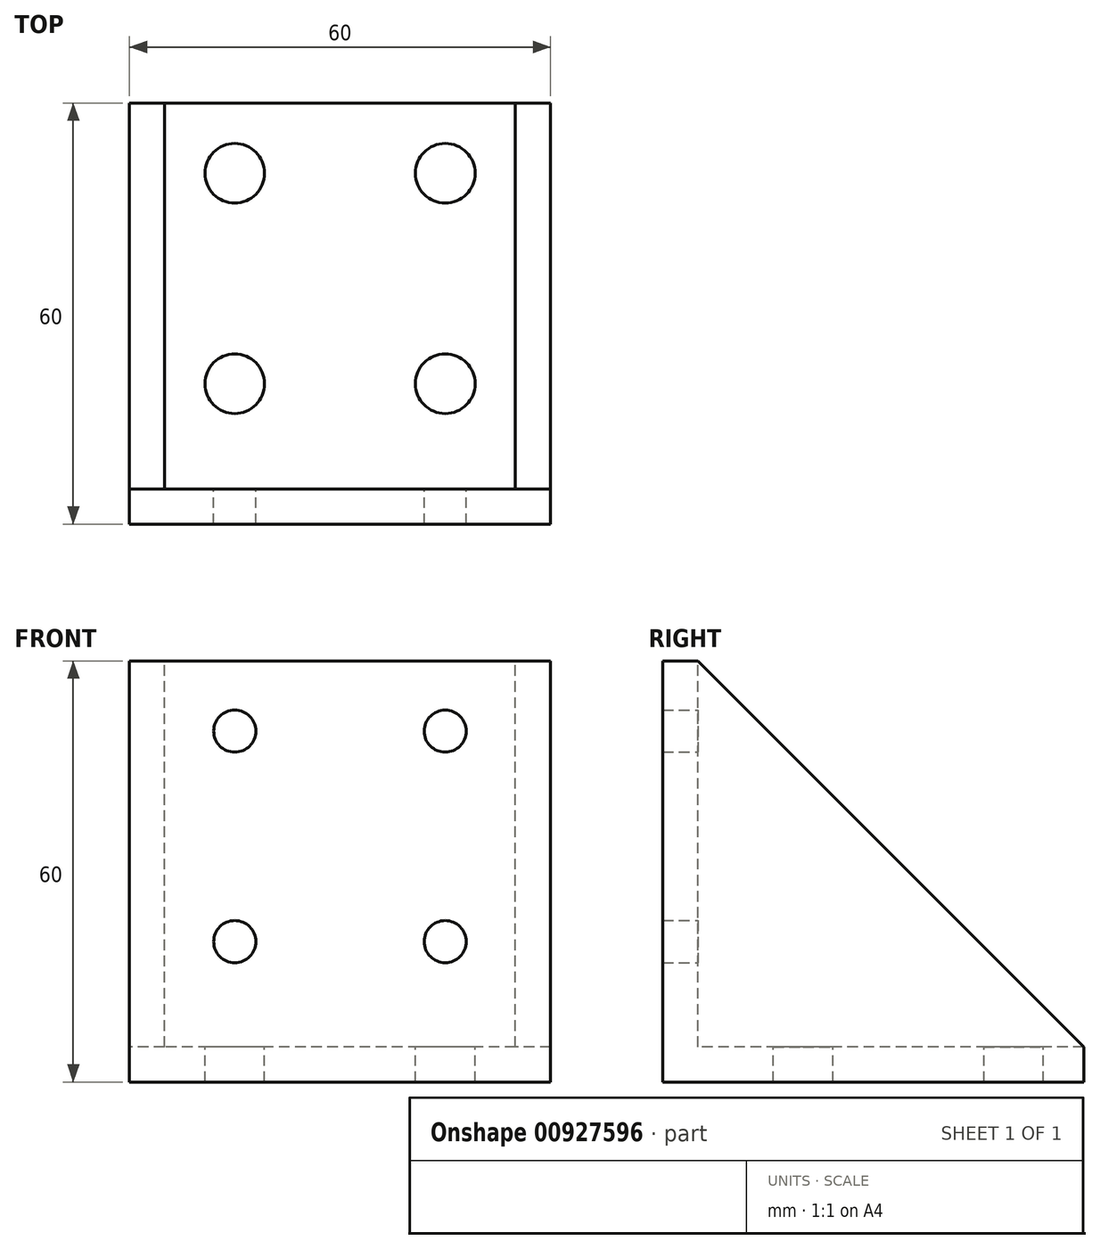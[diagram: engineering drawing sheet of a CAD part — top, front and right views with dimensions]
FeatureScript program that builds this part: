
annotation { "Feature Type Name" : "Feature", "Feature Type Description" : "" }
export const myFeature = defineFeature(function(context is Context, id is Id, definition is map)
    precondition{}
    {
        {
            var Q0;
            Q0=qCreatedBy(makeId("Right.planeOp"),FACE);
            var sketch = newSketch(context, id + "F0", { "sketchPlane" : qUnion([Q0])});
            skLineSegment(sketch, "E0", {"start": v(0, 60) * mm, "end": v(0, 0) * mm});
            skLineSegment(sketch, "E1", {"start": v(0, 0) * mm, "end": v(60, 0) * mm});
            skLineSegment(sketch, "E2.0", {"start": v(5, 60) * mm, "end": v(5, 5) * mm});
            skLineSegment(sketch, "E3.0", {"start": v(5, 5) * mm, "end": v(60, 5) * mm});
            skLineSegment(sketch, "E4", {"start": v(60, 5) * mm, "end": v(60, 0) * mm});
            skLineSegment(sketch, "E5", {"start": v(0, 60) * mm, "end": v(5, 60) * mm});
            skSolve(sketch);
        }
        {
            var Q0;
            Q0 = qSketchRegion(id + "F0", true);
            extrude(context, id + "F1", {"entities" : qUnion([Q0]), "depth" : 60 * mm, "offsetDistance" : 25 * mm});
        }
        {
            var Q0;
            Q0=qCreatedBy(makeId("Right.planeOp"),FACE);
            var sketch = newSketch(context, id + "F2", { "sketchPlane" : qUnion([Q0])});
            skLineSegment(sketch, "E6", {"start": v(5, 60) * mm, "end": v(60, 5) * mm});
            skLineSegment(sketch, "E7", {"start": v(60, 5) * mm, "end": v(5, 5) * mm});
            skLineSegment(sketch, "E8", {"start": v(5, 5) * mm, "end": v(5, 60) * mm});
            skSolve(sketch);
        }
        {
            var Q0;
            Q0 = qSketchRegion(id + "F2", true);
            extrude(context, id + "F3", {"entities" : qUnion([Q0]), "operationType" : NewBodyOperationType.ADD, "depth" : 5 * mm, "offsetDistance" : 25 * mm});
        }
        {
            var Q0;
            Q0=qCreatedBy(makeId("Right.planeOp"),FACE);
            cPlane(context, id + "F4", {"entities" : qUnion([Q0]), "cplaneType" : CPlaneType.OFFSET, "offset" : 60 * mm, "width" : 150 * mm, "height" : 150 * mm});
        }
        {
            var Q0;
            Q0=qCreatedBy(id+"F4.planeOp",FACE);
            var sketch = newSketch(context, id + "F5", { "sketchPlane" : qUnion([Q0])});
            skLineSegment(sketch, "E9", {"start": v(5, 60) * mm, "end": v(60, 5) * mm});
            skLineSegment(sketch, "E10", {"start": v(60, 5) * mm, "end": v(5, 5) * mm});
            skLineSegment(sketch, "E11", {"start": v(5, 5) * mm, "end": v(5, 60) * mm});
            skSolve(sketch);
        }
        {
            var Q0;
            Q0 = qSketchRegion(id + "F5", true);
            extrude(context, id + "F6", {"entities" : qUnion([Q0]), "operationType" : NewBodyOperationType.ADD, "oppositeDirection" : true, "depth" : 5 * mm, "offsetDistance" : 25 * mm});
        }
        {
            var Q0;
            Q0=makeQuery(id+"F1.opExtrude","SWEPT_FACE",FACE,{"disambiguationData":[OSD([sQuery(id+"F0.wireOp",EDGE,"E2.0")])]});
            var sketch = newSketch(context, id + "F7", { "sketchPlane" : qUnion([Q0])});
            skLineSegment(sketch, "E12", {"start": v(-30, 65.9) * mm, "end": v(-30, -13.4) * mm, "construction": true});
            skCircle(sketch, "E13", {"center": v(-15, 50) * mm, "radius": 3 * mm});
            skCircle(sketch, "E14.MirrorC", {"center": v(-45, 50) * mm, "radius": 3 * mm});
            skCircle(sketch, "E15", {"center": v(-15, 20) * mm, "radius": 3 * mm});
            skCircle(sketch, "E16", {"center": v(-45, 20) * mm, "radius": 3 * mm});
            skSolve(sketch);
        }
        {
            var Q0;
            Q0 = qSketchRegion(id + "F7", true);
            extrude(context, id + "F8", {"entities" : qUnion([Q0]), "operationType" : NewBodyOperationType.REMOVE, "endBound" : BoundingType.THROUGH_ALL, "oppositeDirection" : true, "depth" : 25 * mm, "offsetDistance" : 25 * mm});
        }
        {
            var Q0;
            Q0=makeQuery(id+"F1.opExtrude","SWEPT_FACE",FACE,{"disambiguationData":[OSD([sQuery(id+"F0.wireOp",EDGE,"E3.0")])]});
            var sketch = newSketch(context, id + "F9", { "sketchPlane" : qUnion([Q0])});
            skLineSegment(sketch, "E17", {"start": v(30, 67.72) * mm, "end": v(30, -17.54) * mm, "construction": true});
            skPoint(sketch, "E17.startSnap0", {"position": v(30, 60) * mm});
            skPoint(sketch, "E17.endSnap0", {"position": v(30, 5) * mm});
            skCircle(sketch, "E18", {"center": v(45, 50) * mm, "radius": 4.25 * mm});
            skCircle(sketch, "E19.MirrorC", {"center": v(15, 50) * mm, "radius": 4.25 * mm});
            skCircle(sketch, "E20", {"center": v(15, 20) * mm, "radius": 4.25 * mm});
            skCircle(sketch, "E21", {"center": v(45, 20) * mm, "radius": 4.25 * mm});
            skSolve(sketch);
        }
        {
            var Q0;
            Q0 = qSketchRegion(id + "F9", true);
            extrude(context, id + "F10", {"entities" : qUnion([Q0]), "operationType" : NewBodyOperationType.REMOVE, "endBound" : BoundingType.THROUGH_ALL, "oppositeDirection" : true, "depth" : 25 * mm, "offsetDistance" : 25 * mm});
        }
    });
